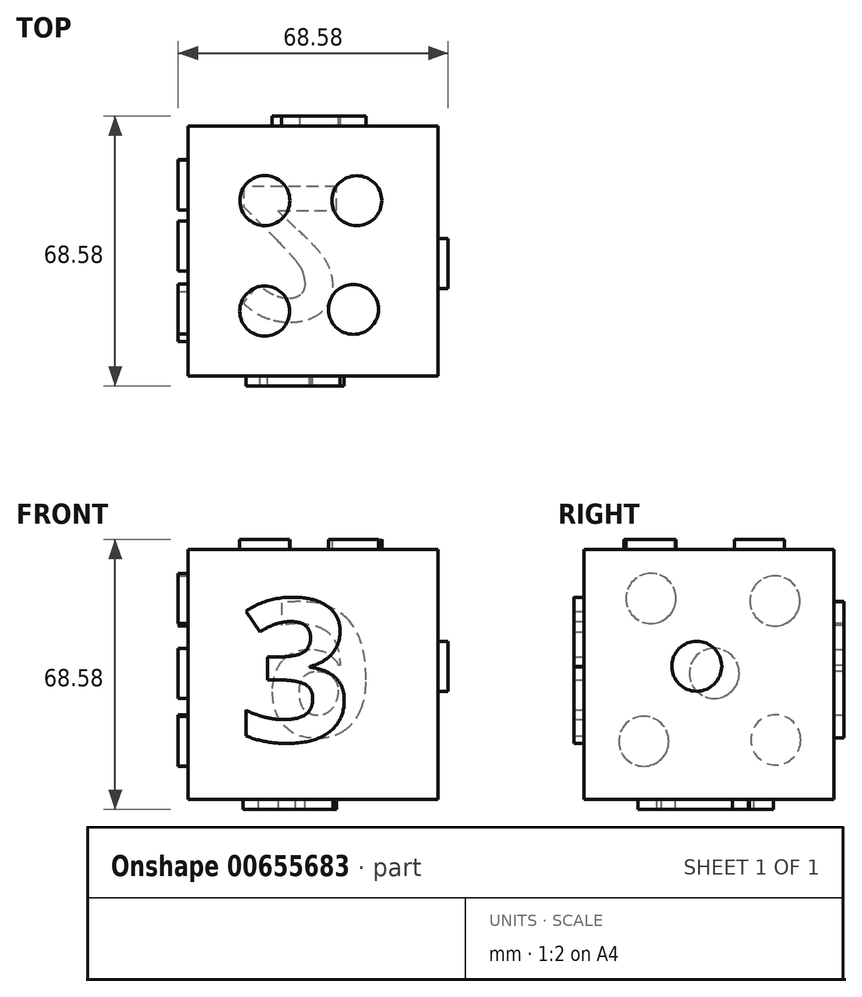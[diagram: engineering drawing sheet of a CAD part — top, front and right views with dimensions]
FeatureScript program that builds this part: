
annotation { "Feature Type Name" : "Feature", "Feature Type Description" : "" }
export const myFeature = defineFeature(function(context is Context, id is Id, definition is map)
    precondition{}
    {
        {
            var Q0;
            Q0=qCreatedBy(makeId("Front.planeOp"),FACE);
            var sketch = newSketch(context, id + "F0", { "sketchPlane" : qUnion([Q0])});
            skLineSegment(sketch, "E0.bottom", {"start": v(-30.34, 25.3) * mm, "end": v(33.16, 25.3) * mm});
            skLineSegment(sketch, "E0.top", {"start": v(-30.34, -38.2) * mm, "end": v(33.16, -38.2) * mm});
            skLineSegment(sketch, "E0.left", {"start": v(-30.34, 25.3) * mm, "end": v(-30.34, -38.2) * mm});
            skLineSegment(sketch, "E0.right", {"start": v(33.16, 25.3) * mm, "end": v(33.16, -38.2) * mm});
            skSolve(sketch);
        }
        {
            var Q0;
            Q0 = qSketchRegion(id + "F0", true);
            extrude(context, id + "F1", {"entities" : qUnion([Q0]), "depth" : 63.5 * mm, "offsetDistance" : 25.4 * mm});
        }
        {
            var Q0;
            Q0=makeQuery(id+"F1.opExtrude","SWEPT_FACE",FACE,{"disambiguationData":[OSD([sQuery(id+"F0.wireOp",EDGE,"E0.left")])]});
            var sketch = newSketch(context, id + "F2", { "sketchPlane" : qUnion([Q0])});
            skCircle(sketch, "E1", {"center": v(14.8, -23.06) * mm, "radius": 6.35 * mm});
            skSolve(sketch);
        }
        {
            var Q0;
            Q0=makeQuery(id+"F2.imprint","IMPRINT",FACE,{"disambiguationData":[TD([[makeQuery(id+"F2.imprint","IMPRINT",EDGE,{"derivedFrom":sQuery(id+"F2.wireOp",EDGE,"E1")}),-1.0]])]});
            var sketch = newSketch(context, id + "F3", { "sketchPlane" : qUnion([Q0])});
            skCircle(sketch, "E2", {"center": v(48.35, -23.43) * mm, "radius": 6.35 * mm});
            skSolve(sketch);
        }
        {
            var Q0;
            Q0=makeQuery(id+"F2.imprint","IMPRINT",FACE,{"disambiguationData":[TD([[makeQuery(id+"F2.imprint","IMPRINT",EDGE,{"derivedFrom":sQuery(id+"F2.wireOp",EDGE,"E1")}),-1.0]])]});
            var sketch = newSketch(context, id + "F4", { "sketchPlane" : qUnion([Q0])});
            skCircle(sketch, "E3", {"center": v(30.44, -6.16) * mm, "radius": 6.35 * mm});
            skSolve(sketch);
        }
        {
            var Q0;
            Q0=makeQuery(id+"F4.imprint","IMPRINT",FACE,{"disambiguationData":[TD([[makeQuery(id+"F4.imprint","IMPRINT",EDGE,{"derivedFrom":sQuery(id+"F4.wireOp",EDGE,"E3")}),-1.0]])]});
            var sketch = newSketch(context, id + "F5", { "sketchPlane" : qUnion([Q0])});
            skCircle(sketch, "E4", {"center": v(46.5, 12.87) * mm, "radius": 6.35 * mm});
            skSolve(sketch);
        }
        {
            var Q0;
            Q0=makeQuery(id+"F5.imprint","IMPRINT",FACE,{"disambiguationData":[TD([[makeQuery(id+"F5.imprint","IMPRINT",EDGE,{"derivedFrom":sQuery(id+"F5.wireOp",EDGE,"E4")}),-1.0]])]});
            var sketch = newSketch(context, id + "F6", { "sketchPlane" : qUnion([Q0])});
            skCircle(sketch, "E5", {"center": v(15.01, 12.24) * mm, "radius": 6.35 * mm});
            skSolve(sketch);
        }
        {
            var Q0;
            Q0 = qSketchRegion(id + "F6", true);
            var Q1;
            Q1 = qSketchRegion(id + "F5", true);
            var Q2;
            Q2 = qSketchRegion(id + "F4", true);
            var Q3;
            Q3 = qSketchRegion(id + "F3", true);
            var Q4;
            Q4 = qSketchRegion(id + "F2", true);
            extrude(context, id + "F7", {"entities" : qUnion([Q0, Q1, Q2, Q3, Q4]), "operationType" : NewBodyOperationType.ADD, "depth" : 2.54 * mm, "offsetDistance" : 25.4 * mm});
        }
        {
            var Q0;
            Q0=makeQuery(id+"F1.opExtrude","CAP_FACE",FACE,{"disambiguationData":[OSD([sQuery(id+"F0.wireOp",EDGE,"E0.bottom"),sQuery(id+"F0.wireOp",EDGE,"E0.top"),sQuery(id+"F0.wireOp",EDGE,"E0.left"),sQuery(id+"F0.wireOp",EDGE,"E0.right")])],"isStart":false});
            var sketch = newSketch(context, id + "F8", { "sketchPlane" : qUnion([Q0])});
            skText(sketch, "E6", { "text": "3\n", "fontName": "OpenSans-Bold.ttf"});
            const initialGuessF8  = {"E6": [-0.01762, -0.02347, 1, 0, 0.03643]};
            skSetInitialGuess(sketch, initialGuessF8);
            skSolve(sketch);
        }
        {
            var Q0;
            Q0 = qSketchRegion(id + "F8", true);
            extrude(context, id + "F9", {"entities" : qUnion([Q0]), "operationType" : NewBodyOperationType.ADD, "depth" : 2.54 * mm, "offsetDistance" : 25.4 * mm});
        }
        {
            var Q0;
            Q0=makeQuery(id+"F1.opExtrude","CAP_FACE",FACE,{"disambiguationData":[OSD([sQuery(id+"F0.wireOp",EDGE,"E0.bottom"),sQuery(id+"F0.wireOp",EDGE,"E0.top"),sQuery(id+"F0.wireOp",EDGE,"E0.left"),sQuery(id+"F0.wireOp",EDGE,"E0.right")])],"isStart":true});
            var sketch = newSketch(context, id + "F10", { "sketchPlane" : qUnion([Q0])});
            skText(sketch, "E7", { "text": "6\n\n", "fontName": "OpenSans-Bold.ttf"});
            const initialGuessF10  = {"E7": [-0.0165, -0.02213, 1, 0, 0.03408]};
            skSetInitialGuess(sketch, initialGuessF10);
            skSolve(sketch);
        }
        {
            var Q0;
            Q0 = qSketchRegion(id + "F10", true);
            extrude(context, id + "F11", {"entities" : qUnion([Q0]), "operationType" : NewBodyOperationType.ADD, "depth" : 2.54 * mm, "offsetDistance" : 25.4 * mm});
        }
        {
            var Q0;
            Q0=makeQuery(id+"F1.opExtrude","SWEPT_FACE",FACE,{"disambiguationData":[OSD([sQuery(id+"F0.wireOp",EDGE,"E0.right")])]});
            var sketch = newSketch(context, id + "F12", { "sketchPlane" : qUnion([Q0])});
            skCircle(sketch, "E8", {"center": v(-34.89, -4.36) * mm, "radius": 6.35 * mm});
            skSolve(sketch);
        }
        {
            var Q0;
            Q0 = qSketchRegion(id + "F12", true);
            extrude(context, id + "F13", {"entities" : qUnion([Q0]), "operationType" : NewBodyOperationType.ADD, "depth" : 2.54 * mm, "offsetDistance" : 25.4 * mm});
        }
        {
            var Q0;
            Q0=makeQuery(id+"F1.opExtrude","SWEPT_FACE",FACE,{"disambiguationData":[OSD([sQuery(id+"F0.wireOp",EDGE,"E0.top")])]});
            var sketch = newSketch(context, id + "F14", { "sketchPlane" : qUnion([Q0])});
            skText(sketch, "E9", { "text": "2", "fontName": "OpenSans-Bold.ttf"});
            const initialGuessF14  = {"E9": [-0.01823, 0.0154, 1, 0, 0.03422]};
            skSetInitialGuess(sketch, initialGuessF14);
            skSolve(sketch);
        }
        {
            var Q0;
            Q0 = qSketchRegion(id + "F14", true);
            extrude(context, id + "F15", {"entities" : qUnion([Q0]), "operationType" : NewBodyOperationType.ADD, "depth" : 2.54 * mm, "offsetDistance" : 25.4 * mm});
        }
        {
            var Q0;
            Q0=makeQuery(id+"F1.opExtrude","SWEPT_FACE",FACE,{"disambiguationData":[OSD([sQuery(id+"F0.wireOp",EDGE,"E0.bottom")])]});
            var sketch = newSketch(context, id + "F16", { "sketchPlane" : qUnion([Q0])});
            skCircle(sketch, "E10", {"center": v(-10.9, -47.01) * mm, "radius": 6.35 * mm});
            skSolve(sketch);
        }
        {
            var Q0;
            Q0=makeQuery(id+"F16.imprint","IMPRINT",FACE,{"disambiguationData":[TD([[makeQuery(id+"F16.imprint","IMPRINT",EDGE,{"derivedFrom":sQuery(id+"F16.wireOp",EDGE,"E10")}),-1.0]])]});
            var sketch = newSketch(context, id + "F17", { "sketchPlane" : qUnion([Q0])});
            skCircle(sketch, "E11", {"center": v(-10.87, -18.93) * mm, "radius": 6.35 * mm});
            skSolve(sketch);
        }
        {
            var Q0;
            Q0=makeQuery(id+"F16.imprint","IMPRINT",FACE,{"disambiguationData":[TD([[makeQuery(id+"F16.imprint","IMPRINT",EDGE,{"derivedFrom":sQuery(id+"F16.wireOp",EDGE,"E10")}),-1.0]])]});
            var sketch = newSketch(context, id + "F18", { "sketchPlane" : qUnion([Q0])});
            skCircle(sketch, "E12", {"center": v(11.65, -46.57) * mm, "radius": 6.35 * mm});
            skSolve(sketch);
        }
        {
            var Q0;
            Q0=makeQuery(id+"F16.imprint","IMPRINT",FACE,{"disambiguationData":[TD([[makeQuery(id+"F16.imprint","IMPRINT",EDGE,{"derivedFrom":sQuery(id+"F16.wireOp",EDGE,"E10")}),-1.0]])]});
            var sketch = newSketch(context, id + "F19", { "sketchPlane" : qUnion([Q0])});
            skCircle(sketch, "E13", {"center": v(12.5, -18.96) * mm, "radius": 6.35 * mm});
            skSolve(sketch);
        }
        {
            var Q0;
            Q0 = qSketchRegion(id + "F19", true);
            var Q1;
            Q1 = qSketchRegion(id + "F18", true);
            var Q2;
            Q2 = qSketchRegion(id + "F17", true);
            var Q3;
            Q3 = qSketchRegion(id + "F16", true);
            extrude(context, id + "F20", {"entities" : qUnion([Q0, Q1, Q2, Q3]), "operationType" : NewBodyOperationType.ADD, "depth" : 2.54 * mm, "offsetDistance" : 25.4 * mm});
        }
    });
